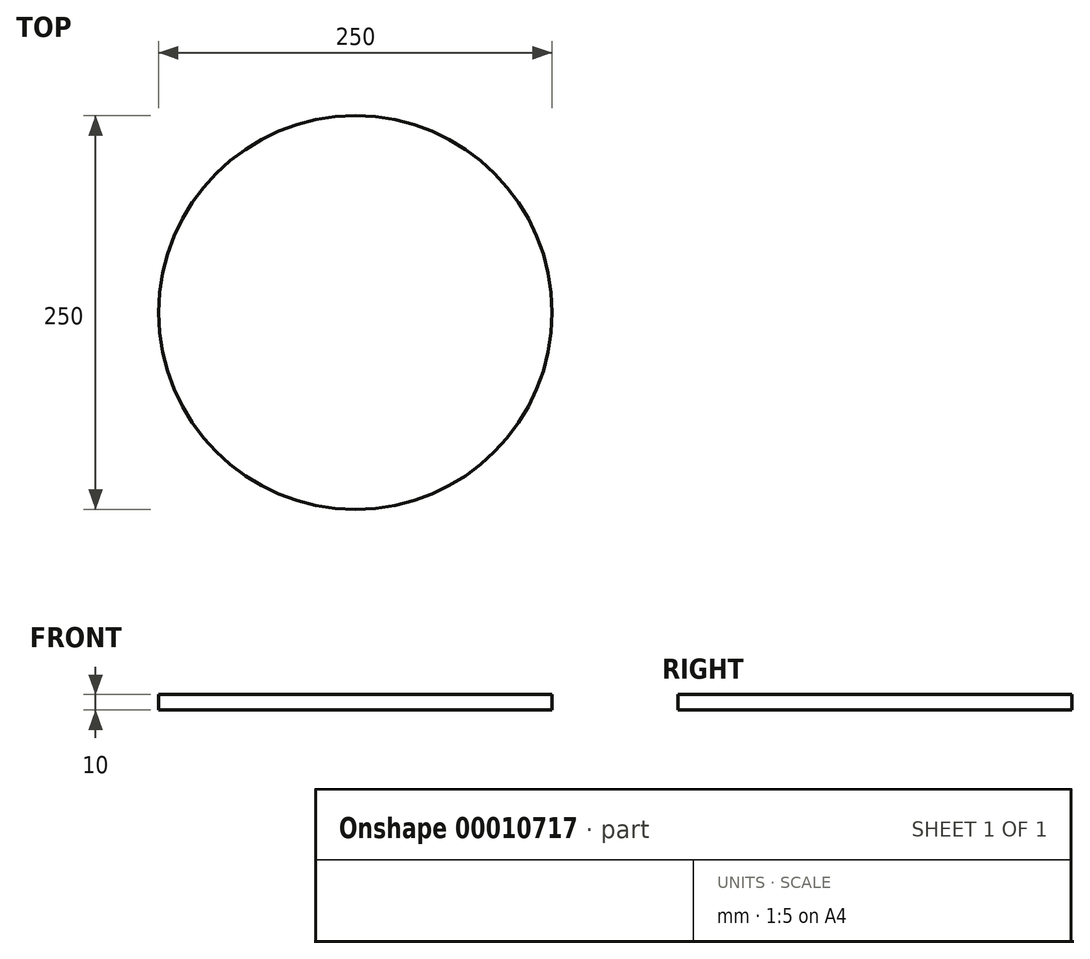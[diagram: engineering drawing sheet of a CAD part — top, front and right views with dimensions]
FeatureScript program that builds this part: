
annotation { "Feature Type Name" : "Feature", "Feature Type Description" : "" }
export const myFeature = defineFeature(function(context is Context, id is Id, definition is map)
    precondition{}
    {
        {
            var Q0;
            Q0=qCreatedBy(makeId("Top.planeOp"),FACE);
            var sketch = newSketch(context, id + "F0", { "sketchPlane" : qUnion([Q0])});
            skCircle(sketch, "E0", {"center": v(0, 0) * mm, "radius": 125 * mm});
            skCircle(sketch, "E1", {"center": v(0, 0) * mm, "radius": 125.55 * mm});
            skSolve(sketch);
        }
        {
            var Q0;
            Q0=makeQuery(id+"F0.imprint","IMPRINT",FACE,{"disambiguationData":[TD([[makeQuery(id+"F0.imprint","IMPRINT",EDGE,{"derivedFrom":sQuery(id+"F0.wireOp",EDGE,"E0")}),1.0]])]});
            extrude(context, id + "F1", {"entities" : qUnion([Q0]), "depth" : 10 * mm});
        }
    });
